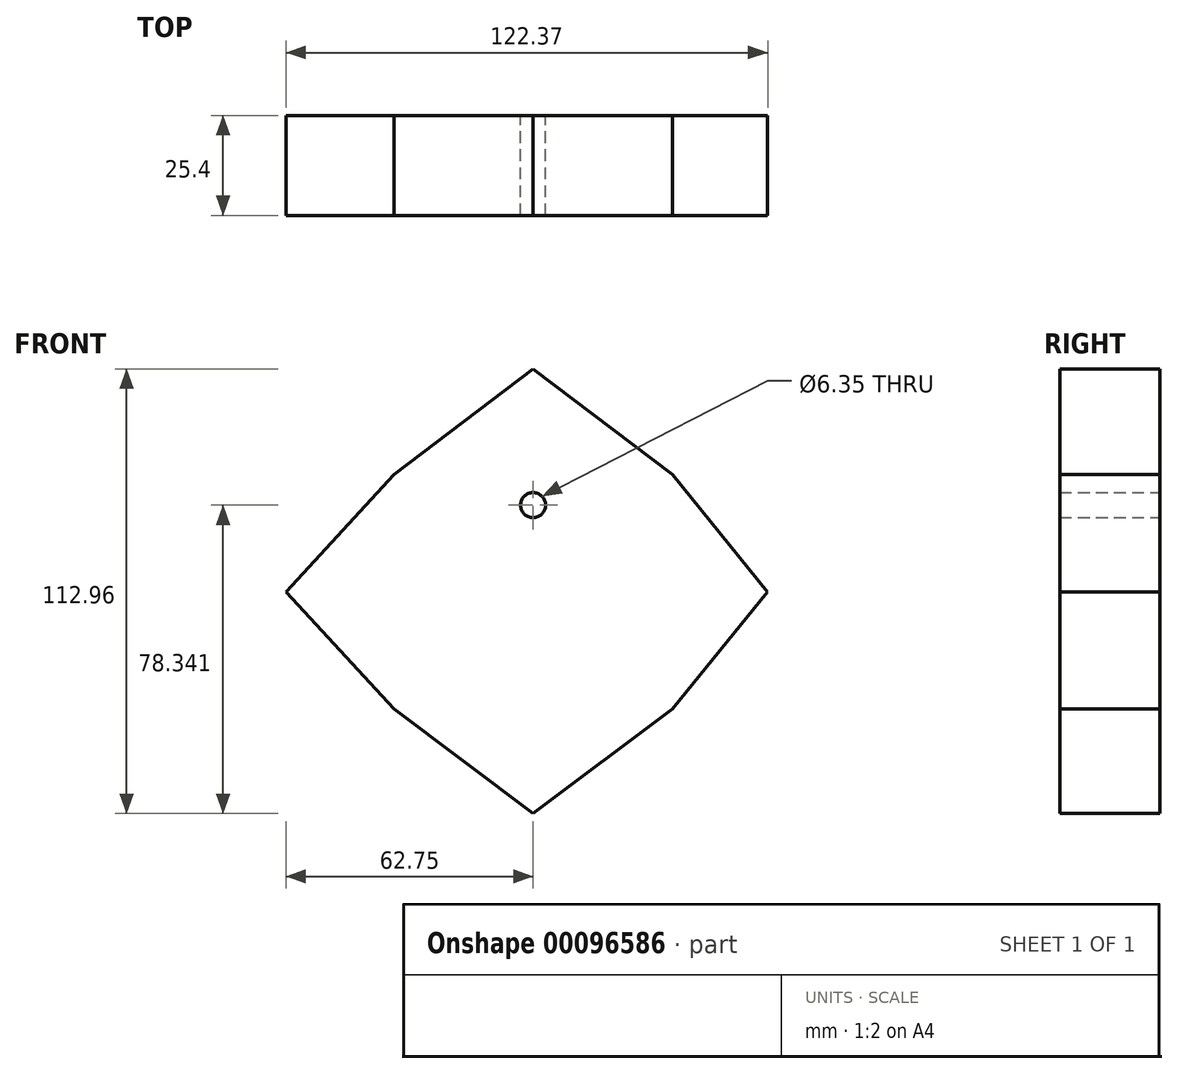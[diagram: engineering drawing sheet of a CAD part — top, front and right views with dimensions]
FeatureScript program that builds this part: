
annotation { "Feature Type Name" : "Feature", "Feature Type Description" : "" }
export const myFeature = defineFeature(function(context is Context, id is Id, definition is map)
    precondition{}
    {
        {
            var Q0;
            Q0=qCreatedBy(makeId("Front.planeOp"),FACE);
            var sketch = newSketch(context, id + "F0", { "sketchPlane" : qUnion([Q0])});
            skLineSegment(sketch, "E0.bottom", {"start": v(-35.37, 29.8) * mm, "end": v(35.37, 29.8) * mm});
            skLineSegment(sketch, "E0.top", {"start": v(-35.37, -29.8) * mm, "end": v(35.37, -29.8) * mm});
            skLineSegment(sketch, "E0.left", {"start": v(-35.37, 29.8) * mm, "end": v(-35.37, -29.8) * mm});
            skLineSegment(sketch, "E0.right", {"start": v(35.37, 29.8) * mm, "end": v(35.37, -29.8) * mm});
            skPoint(sketch, "E0.middle", {"position": v(0, 0) * mm});
            skLineSegment(sketch, "E1", {"start": v(-35.37, 29.8) * mm, "end": v(0, 56.62) * mm});
            skLineSegment(sketch, "E2", {"start": v(0, 56.62) * mm, "end": v(35.37, 29.8) * mm});
            skLineSegment(sketch, "E3", {"start": v(35.37, -29.8) * mm, "end": v(0, -56.34) * mm});
            skLineSegment(sketch, "E4", {"start": v(0, -56.34) * mm, "end": v(-35.37, -29.8) * mm});
            skLineSegment(sketch, "E5", {"start": v(35.37, 29.8) * mm, "end": v(59.62, 0) * mm});
            skLineSegment(sketch, "E6", {"start": v(59.62, 0) * mm, "end": v(35.37, -29.8) * mm});
            skLineSegment(sketch, "E7", {"start": v(-35.37, 29.8) * mm, "end": v(-62.75, 0) * mm});
            skLineSegment(sketch, "E8", {"start": v(-62.75, 0) * mm, "end": v(-35.37, -29.8) * mm});
            skSolve(sketch);
        }
        {
            var Q0;
            Q0 = qSketchRegion(id + "F0", true);
            extrude(context, id + "F1", {"entities" : qUnion([Q0]), "depth" : 25.4 * mm});
        }
        {
            var Q0;
            Q0=qCreatedBy(makeId("Front.planeOp"),FACE);
            var sketch = newSketch(context, id + "F2", { "sketchPlane" : qUnion([Q0])});
            skCircle(sketch, "E9", {"center": v(0, 0) * mm, "radius": 16.44 * mm});
            skSolve(sketch);
        }
        {
            var Q0;
            Q0 = qSketchRegion(id + "F2", true);
            extrude(context, id + "F3", {"entities" : qUnion([Q0]), "operationType" : NewBodyOperationType.ADD, "depth" : 25.4 * mm});
        }
        {
            var Q0;
            Q0=qCreatedBy(makeId("Front.planeOp"),FACE);
            var sketch = newSketch(context, id + "F4", { "sketchPlane" : qUnion([Q0])});
            skCircle(sketch, "E10", {"center": v(0, 0) * mm, "radius": 22 * mm});
            skCircle(sketch, "E11", {"center": v(0, 22) * mm, "radius": 12.7 * mm});
            skCircle(sketch, "E12", {"center": v(0, -22) * mm, "radius": 12.7 * mm});
            skCircle(sketch, "E13", {"center": v(22, 0) * mm, "radius": 12.7 * mm});
            skCircle(sketch, "E14", {"center": v(-22, 0) * mm, "radius": 12.7 * mm});
            skSolve(sketch);
        }
        {
            var Q0;
            Q0=sQuery(id+"F4.wireOp",VERTEX,"E11.center");
            var Q1;
            Q1=makeQuery(id+"F1.opExtrude","SWEPT_BODY",BODY,{"disambiguationData":[OSD([sQuery(id+"F0.wireOp",EDGE,"E1"),sQuery(id+"F0.wireOp",EDGE,"E2"),sQuery(id+"F0.wireOp",EDGE,"E3"),sQuery(id+"F0.wireOp",EDGE,"E4"),sQuery(id+"F0.wireOp",EDGE,"E5"),sQuery(id+"F0.wireOp",EDGE,"E6"),sQuery(id+"F0.wireOp",EDGE,"E7"),sQuery(id+"F0.wireOp",EDGE,"E8")])]});
            hole(context, id + "F5", {"style" : HoleStyle.SIMPLE, "endStyle" : HoleEndStyle.THROUGH, "oppositeDirection" : true, "holeDiameter" : 6.35 * mm, "locations" : qUnion([Q0]), "scope" : qUnion([Q1]), "isTappedThrough" : true});
        }
    });
